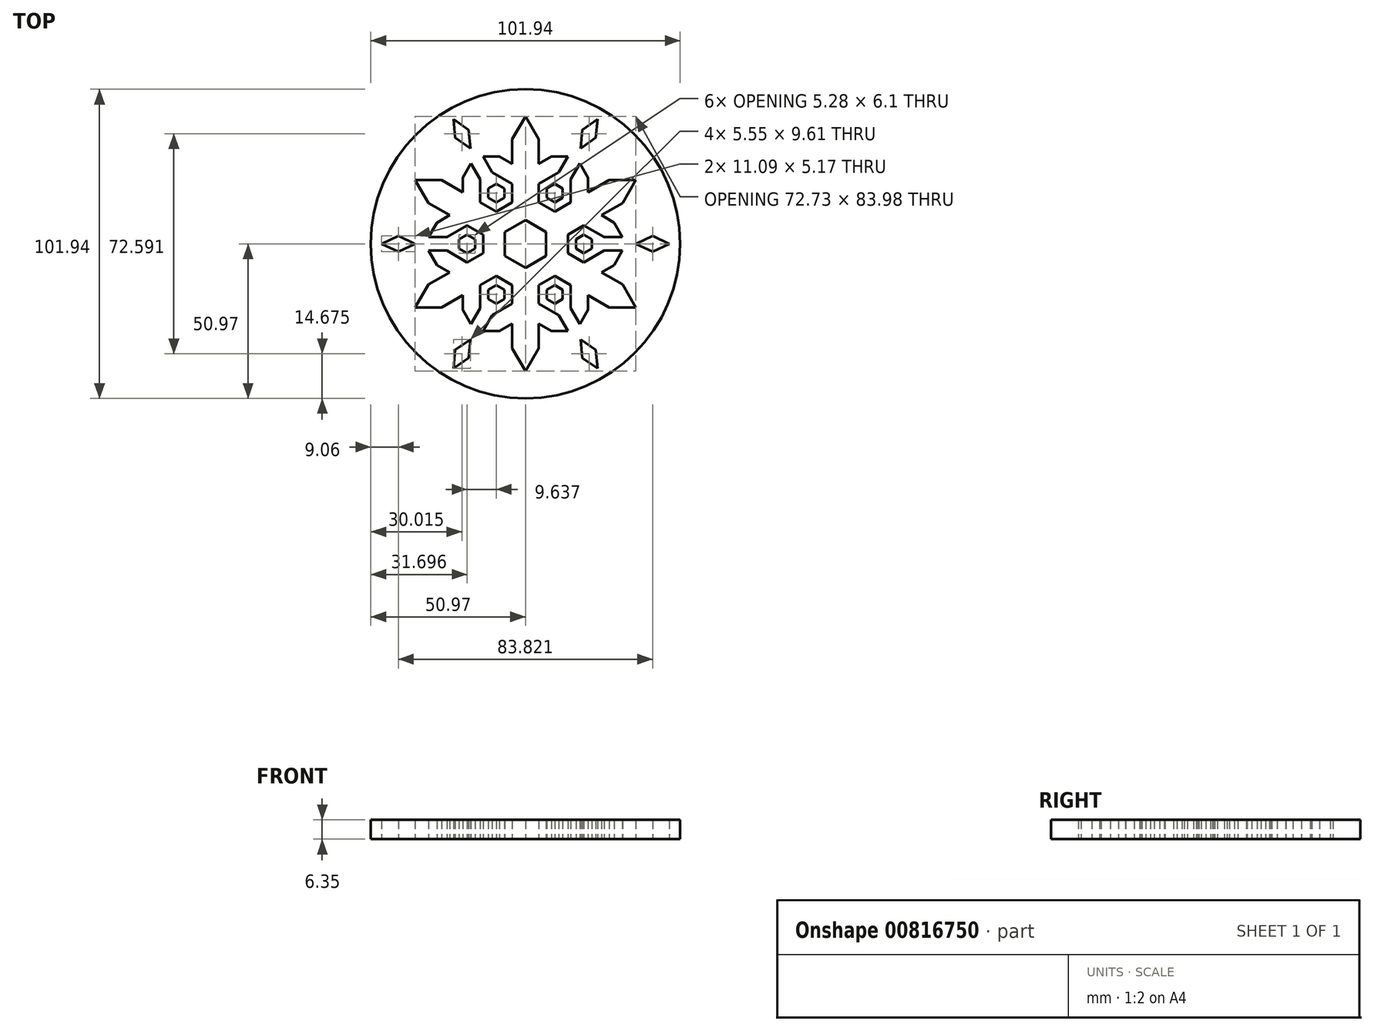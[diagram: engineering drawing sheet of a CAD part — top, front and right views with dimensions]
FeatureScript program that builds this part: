
annotation { "Feature Type Name" : "Feature", "Feature Type Description" : "" }
export const myFeature = defineFeature(function(context is Context, id is Id, definition is map)
    precondition{}
    {
        {
            var Q0;
            Q0=qCreatedBy(makeId("Top.planeOp"),FACE);
            var sketch = newSketch(context, id + "F0", { "sketchPlane" : qUnion([Q0])});
            skCircle(sketch, "E0.cCircle", {"center": v(0, 0) * mm, "radius": 41.99 * mm, "construction": true});
            skLineSegment(sketch, "E0.0", {"start": v(0, 41.99) * mm, "end": v(36.36, 21) * mm, "construction": true});
            skLineSegment(sketch, "E0.1", {"start": v(36.36, 21) * mm, "end": v(36.36, -21) * mm, "construction": true});
            skLineSegment(sketch, "E0.2", {"start": v(36.36, -21) * mm, "end": v(0, -41.99) * mm, "construction": true});
            skLineSegment(sketch, "E0.3", {"start": v(0, -41.99) * mm, "end": v(-36.36, -21) * mm, "construction": true});
            skLineSegment(sketch, "E0.4", {"start": v(-36.36, -21) * mm, "end": v(-36.36, 21) * mm, "construction": true});
            skLineSegment(sketch, "E0.5", {"start": v(-36.36, 21) * mm, "end": v(0, 41.99) * mm, "construction": true});
            skLineSegment(sketch, "E1", {"start": v(0, 41.99) * mm, "end": v(-4.36, 34.44) * mm});
            skLineSegment(sketch, "E2", {"start": v(-4.36, 34.44) * mm, "end": v(-4.36, 26.36) * mm});
            skLineSegment(sketch, "E3", {"start": v(-4.36, 26.36) * mm, "end": v(-8.55, 28.78) * mm});
            skLineSegment(sketch, "E4", {"start": v(-8.55, 28.78) * mm, "end": v(-14, 28.78) * mm});
            skLineSegment(sketch, "E5", {"start": v(-14, 28.78) * mm, "end": v(-10.98, 23.56) * mm});
            skLineSegment(sketch, "E6", {"start": v(-10.98, 23.56) * mm, "end": v(-4.36, 19.74) * mm});
            skLineSegment(sketch, "E7", {"start": v(-4.36, 19.74) * mm, "end": v(-4.36, 13.64) * mm});
            skLineSegment(sketch, "E8", {"start": v(0, 50.97) * mm, "end": v(0, -50.97) * mm, "construction": true});
            skLineSegment(sketch, "E9.MirrorCS", {"start": v(0, 41.99) * mm, "end": v(4.36, 34.44) * mm});
            skLineSegment(sketch, "E10.MirrorCS", {"start": v(4.36, 34.44) * mm, "end": v(4.36, 26.36) * mm});
            skLineSegment(sketch, "E11.MirrorCS", {"start": v(4.36, 26.36) * mm, "end": v(8.55, 28.78) * mm});
            skLineSegment(sketch, "E12.MirrorCS", {"start": v(8.55, 28.78) * mm, "end": v(14, 28.78) * mm});
            skLineSegment(sketch, "E13.MirrorCS", {"start": v(14, 28.78) * mm, "end": v(10.98, 23.56) * mm});
            skLineSegment(sketch, "E14.MirrorCS", {"start": v(4.36, 19.74) * mm, "end": v(4.36, 13.64) * mm});
            skLineSegment(sketch, "E15.MirrorCS", {"start": v(10.98, 23.56) * mm, "end": v(4.36, 19.74) * mm});
            skLineSegment(sketch, "E16", {"start": v(-25.48, -44.14) * mm, "end": v(25.48, 44.14) * mm, "construction": true});
            skLineSegment(sketch, "E17", {"start": v(-50.97, 0) * mm, "end": v(50.97, 0) * mm, "construction": true});
            skLineSegment(sketch, "E18", {"start": v(-25.48, 44.14) * mm, "end": v(25.48, -44.14) * mm, "construction": true});
            skLineSegment(sketch, "E19.MirrorCS", {"start": v(25, 9.4) * mm, "end": v(29.2, 6.99) * mm});
            skLineSegment(sketch, "E20.MirrorCS", {"start": v(25.9, 2.27) * mm, "end": v(19.27, 6.1) * mm});
            skLineSegment(sketch, "E21.MirrorCS", {"start": v(31.92, 2.27) * mm, "end": v(25.9, 2.27) * mm});
            skLineSegment(sketch, "E22.MirrorCS", {"start": v(36.36, 21) * mm, "end": v(27.65, 21) * mm});
            skLineSegment(sketch, "E23.MirrorCS", {"start": v(17.93, 26.5) * mm, "end": v(14.92, 21.3) * mm});
            skLineSegment(sketch, "E24.MirrorCS", {"start": v(20.65, 16.95) * mm, "end": v(20.65, 21.8) * mm});
            skLineSegment(sketch, "E25.MirrorCS", {"start": v(36.36, 21) * mm, "end": v(32, 13.45) * mm});
            skLineSegment(sketch, "E26.MirrorCS", {"start": v(20.65, 21.8) * mm, "end": v(17.93, 26.5) * mm});
            skLineSegment(sketch, "E27.MirrorCS", {"start": v(29.2, 6.99) * mm, "end": v(31.92, 2.27) * mm});
            skLineSegment(sketch, "E28.MirrorCS", {"start": v(14.92, 13.64) * mm, "end": v(9.64, 10.6) * mm});
            skLineSegment(sketch, "E29.MirrorCS", {"start": v(19.27, 6.1) * mm, "end": v(14, 3.05) * mm});
            skLineSegment(sketch, "E30.MirrorCS", {"start": v(14.92, 21.3) * mm, "end": v(14.92, 13.64) * mm});
            skLineSegment(sketch, "E31.MirrorCS", {"start": v(32, 13.45) * mm, "end": v(25, 9.4) * mm});
            skLineSegment(sketch, "E32.MirrorCS", {"start": v(27.65, 21) * mm, "end": v(20.65, 16.95) * mm});
            skLineSegment(sketch, "E33.MirrorCS", {"start": v(25, -9.4) * mm, "end": v(29.2, -6.99) * mm});
            skLineSegment(sketch, "E34.MirrorCS", {"start": v(27.65, -21) * mm, "end": v(20.65, -16.95) * mm});
            skLineSegment(sketch, "E35.MirrorCS", {"start": v(36.36, -21) * mm, "end": v(32, -13.45) * mm});
            skLineSegment(sketch, "E36.MirrorCS", {"start": v(31.92, -2.27) * mm, "end": v(25.9, -2.27) * mm});
            skLineSegment(sketch, "E37.MirrorCS", {"start": v(14.92, -13.64) * mm, "end": v(9.64, -10.6) * mm});
            skLineSegment(sketch, "E38.MirrorCS", {"start": v(17.93, -26.5) * mm, "end": v(14.92, -21.3) * mm});
            skLineSegment(sketch, "E39.MirrorCS", {"start": v(14.92, -21.3) * mm, "end": v(14.92, -13.64) * mm});
            skLineSegment(sketch, "E40.MirrorCS", {"start": v(25.9, -2.27) * mm, "end": v(19.27, -6.1) * mm});
            skLineSegment(sketch, "E41.MirrorCS", {"start": v(19.27, -6.1) * mm, "end": v(14, -3.05) * mm});
            skLineSegment(sketch, "E42.MirrorCS", {"start": v(20.65, -16.95) * mm, "end": v(20.65, -21.8) * mm});
            skLineSegment(sketch, "E43.MirrorCS", {"start": v(32, -13.45) * mm, "end": v(25, -9.4) * mm});
            skLineSegment(sketch, "E44.MirrorCS", {"start": v(20.65, -21.8) * mm, "end": v(17.93, -26.5) * mm});
            skLineSegment(sketch, "E45.MirrorCS", {"start": v(36.36, -21) * mm, "end": v(27.65, -21) * mm});
            skLineSegment(sketch, "E46.MirrorCS", {"start": v(29.2, -6.99) * mm, "end": v(31.92, -2.27) * mm});
            skLineSegment(sketch, "E47.MirrorCS", {"start": v(-4.36, -26.36) * mm, "end": v(-8.55, -28.78) * mm});
            skLineSegment(sketch, "E48.MirrorCS", {"start": v(-25, 9.4) * mm, "end": v(-29.2, 6.99) * mm});
            skLineSegment(sketch, "E49.MirrorCS", {"start": v(0, -41.99) * mm, "end": v(-4.36, -34.44) * mm});
            skLineSegment(sketch, "E50.MirrorCS", {"start": v(4.36, -26.36) * mm, "end": v(8.55, -28.78) * mm});
            skLineSegment(sketch, "E51.MirrorCS", {"start": v(-14.92, -21.3) * mm, "end": v(-14.92, -13.64) * mm});
            skLineSegment(sketch, "E52.MirrorCS", {"start": v(-31.92, 2.27) * mm, "end": v(-25.9, 2.27) * mm});
            skLineSegment(sketch, "E53.MirrorCS", {"start": v(8.55, -28.78) * mm, "end": v(14, -28.78) * mm});
            skLineSegment(sketch, "E54.MirrorCS", {"start": v(-20.65, -21.8) * mm, "end": v(-17.93, -26.5) * mm});
            skLineSegment(sketch, "E55.MirrorCS", {"start": v(4.36, -34.44) * mm, "end": v(4.36, -26.36) * mm});
            skLineSegment(sketch, "E56.MirrorCS", {"start": v(-29.2, 6.99) * mm, "end": v(-31.92, 2.27) * mm});
            skLineSegment(sketch, "E57.MirrorCS", {"start": v(-20.65, -16.95) * mm, "end": v(-20.65, -21.8) * mm});
            skLineSegment(sketch, "E58.MirrorCS", {"start": v(-4.36, -34.44) * mm, "end": v(-4.36, -26.36) * mm});
            skLineSegment(sketch, "E59.MirrorCS", {"start": v(-14, -28.78) * mm, "end": v(-10.98, -23.56) * mm});
            skLineSegment(sketch, "E60.MirrorCS", {"start": v(-17.93, -26.5) * mm, "end": v(-14.92, -21.3) * mm});
            skLineSegment(sketch, "E61.MirrorCS", {"start": v(14, -28.78) * mm, "end": v(10.98, -23.56) * mm});
            skLineSegment(sketch, "E62.MirrorCS", {"start": v(-31.92, -2.27) * mm, "end": v(-25.9, -2.27) * mm});
            skLineSegment(sketch, "E63.MirrorCS", {"start": v(0, -41.99) * mm, "end": v(4.36, -34.44) * mm});
            skLineSegment(sketch, "E64.MirrorCS", {"start": v(-32, 13.45) * mm, "end": v(-25, 9.4) * mm});
            skLineSegment(sketch, "E65.MirrorCS", {"start": v(-10.98, -23.56) * mm, "end": v(-4.36, -19.74) * mm});
            skLineSegment(sketch, "E66.MirrorCS", {"start": v(-25.9, 2.27) * mm, "end": v(-19.27, 6.1) * mm});
            skLineSegment(sketch, "E67.MirrorCS", {"start": v(-36.36, -21) * mm, "end": v(-32, -13.45) * mm});
            skLineSegment(sketch, "E68.MirrorCS", {"start": v(-17.93, 26.5) * mm, "end": v(-14.92, 21.3) * mm});
            skLineSegment(sketch, "E69.MirrorCS", {"start": v(-20.65, 21.8) * mm, "end": v(-17.93, 26.5) * mm});
            skLineSegment(sketch, "E70.MirrorCS", {"start": v(-20.65, 16.95) * mm, "end": v(-20.65, 21.8) * mm});
            skLineSegment(sketch, "E71.MirrorCS", {"start": v(-36.36, 21) * mm, "end": v(-27.65, 21) * mm});
            skLineSegment(sketch, "E72.MirrorCS", {"start": v(-14.92, 21.3) * mm, "end": v(-14.92, 13.64) * mm});
            skLineSegment(sketch, "E73.MirrorCS", {"start": v(-36.36, -21) * mm, "end": v(-27.65, -21) * mm});
            skLineSegment(sketch, "E74.MirrorCS", {"start": v(-36.36, 21) * mm, "end": v(-32, 13.45) * mm});
            skLineSegment(sketch, "E75.MirrorCS", {"start": v(-27.65, -21) * mm, "end": v(-20.65, -16.95) * mm});
            skLineSegment(sketch, "E76.MirrorCS", {"start": v(-27.65, 21) * mm, "end": v(-20.65, 16.95) * mm});
            skLineSegment(sketch, "E77.MirrorCS", {"start": v(-25, -9.4) * mm, "end": v(-29.2, -6.99) * mm});
            skLineSegment(sketch, "E78.MirrorCS", {"start": v(-29.2, -6.99) * mm, "end": v(-31.92, -2.27) * mm});
            skLineSegment(sketch, "E79.MirrorCS", {"start": v(-32, -13.45) * mm, "end": v(-25, -9.4) * mm});
            skLineSegment(sketch, "E80.MirrorCS", {"start": v(-8.55, -28.78) * mm, "end": v(-14, -28.78) * mm});
            skLineSegment(sketch, "E81.MirrorCS", {"start": v(-14.92, -13.64) * mm, "end": v(-9.64, -10.6) * mm});
            skLineSegment(sketch, "E82.MirrorCS", {"start": v(-19.27, -6.1) * mm, "end": v(-14, -3.05) * mm});
            skLineSegment(sketch, "E83.MirrorCS", {"start": v(-19.27, 6.1) * mm, "end": v(-14, 3.05) * mm});
            skLineSegment(sketch, "E84.MirrorCS", {"start": v(-25.9, -2.27) * mm, "end": v(-19.27, -6.1) * mm});
            skLineSegment(sketch, "E85.MirrorCS", {"start": v(4.36, -19.74) * mm, "end": v(4.36, -13.64) * mm});
            skLineSegment(sketch, "E86.MirrorCS", {"start": v(-4.36, -19.74) * mm, "end": v(-4.36, -13.64) * mm});
            skLineSegment(sketch, "E87.MirrorCS", {"start": v(-14.92, 13.64) * mm, "end": v(-9.64, 10.6) * mm});
            skLineSegment(sketch, "E88.MirrorCS", {"start": v(10.98, -23.56) * mm, "end": v(4.36, -19.74) * mm});
            skCircle(sketch, "E89", {"center": v(0, 0) * mm, "radius": 50.97 * mm});
            skLineSegment(sketch, "E90.0", {"start": v(4.36, 13.64) * mm, "end": v(9.64, 10.6) * mm});
            skLineSegment(sketch, "E90.1", {"start": v(14, 3.05) * mm, "end": v(14, -3.05) * mm});
            skLineSegment(sketch, "E90.2", {"start": v(9.64, -10.6) * mm, "end": v(4.36, -13.64) * mm});
            skLineSegment(sketch, "E90.3", {"start": v(-4.36, -13.64) * mm, "end": v(-9.64, -10.6) * mm});
            skLineSegment(sketch, "E90.4", {"start": v(-14, -3.05) * mm, "end": v(-14, 3.05) * mm});
            skLineSegment(sketch, "E90.5", {"start": v(-9.64, 10.6) * mm, "end": v(-4.36, 13.64) * mm});
            skLineSegment(sketch, "E91.0", {"start": v(0, 7.87) * mm, "end": v(6.81, 3.93) * mm});
            skLineSegment(sketch, "E91.1", {"start": v(6.81, 3.93) * mm, "end": v(6.81, -3.93) * mm});
            skLineSegment(sketch, "E91.2", {"start": v(6.81, -3.93) * mm, "end": v(0, -7.87) * mm});
            skLineSegment(sketch, "E91.3", {"start": v(0, -7.87) * mm, "end": v(-6.81, -3.93) * mm});
            skLineSegment(sketch, "E91.4", {"start": v(-6.81, -3.93) * mm, "end": v(-6.81, 3.93) * mm});
            skLineSegment(sketch, "E91.5", {"start": v(-6.81, 3.93) * mm, "end": v(0, 7.87) * mm});
            skLineSegment(sketch, "E92", {"start": v(-18.18, -31.5) * mm, "end": v(-18.72, -37.59) * mm});
            skLineSegment(sketch, "E93", {"start": v(-18.72, -37.59) * mm, "end": v(-23.73, -41.1) * mm});
            skLineSegment(sketch, "E94", {"start": v(-23.73, -41.1) * mm, "end": v(-23.2, -35) * mm});
            skLineSegment(sketch, "E95", {"start": v(-23.2, -35) * mm, "end": v(-18.18, -31.5) * mm});
            skLineSegment(sketch, "E96.MirrorCS", {"start": v(23.2, -35) * mm, "end": v(18.18, -31.5) * mm});
            skLineSegment(sketch, "E97.MirrorCS", {"start": v(18.18, -31.5) * mm, "end": v(18.72, -37.59) * mm});
            skLineSegment(sketch, "E98.MirrorCS", {"start": v(18.72, -37.59) * mm, "end": v(23.73, -41.1) * mm});
            skLineSegment(sketch, "E99.MirrorCS", {"start": v(23.73, -41.1) * mm, "end": v(23.2, -35) * mm});
            skLineSegment(sketch, "E100", {"start": v(-36.36, 21) * mm, "end": v(36.36, -21) * mm, "construction": true});
            skLineSegment(sketch, "E101.MirrorCS", {"start": v(41.91, -2.59) * mm, "end": v(36.36, 0) * mm});
            skLineSegment(sketch, "E102.MirrorCS", {"start": v(36.36, 0) * mm, "end": v(41.91, 2.59) * mm});
            skLineSegment(sketch, "E103.MirrorCS", {"start": v(41.91, 2.59) * mm, "end": v(47.46, 0) * mm});
            skLineSegment(sketch, "E104.MirrorCS", {"start": v(47.46, 0) * mm, "end": v(41.91, -2.59) * mm});
            skLineSegment(sketch, "E105", {"start": v(-36.36, -21) * mm, "end": v(36.36, 21) * mm, "construction": true});
            skLineSegment(sketch, "E106.MirrorCS", {"start": v(23.2, 35) * mm, "end": v(23.73, 41.1) * mm});
            skLineSegment(sketch, "E107.MirrorCS", {"start": v(18.18, 31.5) * mm, "end": v(23.2, 35) * mm});
            skLineSegment(sketch, "E108.MirrorCS", {"start": v(18.72, 37.59) * mm, "end": v(18.18, 31.5) * mm});
            skLineSegment(sketch, "E109.MirrorCS", {"start": v(23.73, 41.1) * mm, "end": v(18.72, 37.59) * mm});
            skLineSegment(sketch, "E110.MirrorCS", {"start": v(-23.73, 41.1) * mm, "end": v(-18.72, 37.59) * mm});
            skLineSegment(sketch, "E111.MirrorCS", {"start": v(-18.72, 37.59) * mm, "end": v(-18.18, 31.5) * mm});
            skLineSegment(sketch, "E112.MirrorCS", {"start": v(-18.18, 31.5) * mm, "end": v(-23.2, 35) * mm});
            skLineSegment(sketch, "E113.MirrorCS", {"start": v(-23.2, 35) * mm, "end": v(-23.73, 41.1) * mm});
            skLineSegment(sketch, "E114.MirrorCS", {"start": v(-36.36, 0) * mm, "end": v(-41.91, 2.59) * mm});
            skLineSegment(sketch, "E115.MirrorCS", {"start": v(-41.91, -2.59) * mm, "end": v(-36.36, 0) * mm});
            skLineSegment(sketch, "E116.MirrorCS", {"start": v(-47.46, 0) * mm, "end": v(-41.91, -2.59) * mm});
            skLineSegment(sketch, "E117.MirrorCS", {"start": v(-41.91, 2.59) * mm, "end": v(-47.46, 0) * mm});
            skLineSegment(sketch, "E118", {"start": v(-4.36, 34.44) * mm, "end": v(-27.65, 21) * mm, "construction": true});
            skLineSegment(sketch, "E119", {"start": v(-4.36, 19.74) * mm, "end": v(-14.92, 13.64) * mm, "construction": true});
            skCircle(sketch, "E120.cCircle", {"center": v(-9.64, 16.7) * mm, "radius": 3.05 * mm, "construction": true});
            skLineSegment(sketch, "E120.0", {"start": v(-7, 18.22) * mm, "end": v(-7, 15.17) * mm});
            skLineSegment(sketch, "E120.1", {"start": v(-7, 15.17) * mm, "end": v(-9.64, 13.64) * mm});
            skLineSegment(sketch, "E120.2", {"start": v(-9.64, 13.64) * mm, "end": v(-12.28, 15.17) * mm});
            skLineSegment(sketch, "E120.3", {"start": v(-12.28, 15.17) * mm, "end": v(-12.28, 18.22) * mm});
            skLineSegment(sketch, "E120.4", {"start": v(-12.28, 18.22) * mm, "end": v(-9.64, 19.74) * mm});
            skLineSegment(sketch, "E120.5", {"start": v(-9.64, 19.74) * mm, "end": v(-7, 18.22) * mm});
            skCircle(sketch, "E121.MirrorC", {"center": v(19.27, 0) * mm, "radius": 3.05 * mm, "construction": true});
            skLineSegment(sketch, "E122.MirrorCS", {"start": v(19.27, 3.05) * mm, "end": v(16.63, 1.52) * mm});
            skLineSegment(sketch, "E123.MirrorCS", {"start": v(16.63, -1.52) * mm, "end": v(19.27, -3.05) * mm});
            skLineSegment(sketch, "E124.MirrorCS", {"start": v(16.63, 1.52) * mm, "end": v(16.63, -1.52) * mm});
            skLineSegment(sketch, "E125.MirrorCS", {"start": v(19.27, -3.05) * mm, "end": v(21.91, -1.52) * mm});
            skLineSegment(sketch, "E126.MirrorCS", {"start": v(21.91, -1.52) * mm, "end": v(21.91, 1.52) * mm});
            skLineSegment(sketch, "E127.MirrorCS", {"start": v(21.91, 1.52) * mm, "end": v(19.27, 3.05) * mm});
            skLineSegment(sketch, "E128.MirrorCS", {"start": v(19.27, 6.1) * mm, "end": v(19.27, -6.1) * mm, "construction": true});
            skLineSegment(sketch, "E129", {"start": v(4.36, 19.74) * mm, "end": v(14.92, 13.64) * mm, "construction": true});
            skLineSegment(sketch, "E130", {"start": v(14.92, -13.64) * mm, "end": v(4.36, -19.74) * mm, "construction": true});
            skLineSegment(sketch, "E131", {"start": v(-4.36, -19.74) * mm, "end": v(-14.92, -13.64) * mm, "construction": true});
            skLineSegment(sketch, "E132", {"start": v(-19.27, -6.1) * mm, "end": v(-19.27, 6.1) * mm, "construction": true});
            skLineSegment(sketch, "E133", {"start": v(-9.64, 16.7) * mm, "end": v(-9.64, 10.6) * mm, "construction": true});
            skCircle(sketch, "E134.cCircle", {"center": v(9.64, 16.7) * mm, "radius": 2.64 * mm, "construction": true});
            skLineSegment(sketch, "E134.0", {"start": v(9.64, 19.74) * mm, "end": v(12.28, 18.22) * mm});
            skLineSegment(sketch, "E134.1", {"start": v(12.28, 18.22) * mm, "end": v(12.28, 15.17) * mm});
            skLineSegment(sketch, "E134.2", {"start": v(12.28, 15.17) * mm, "end": v(9.64, 13.64) * mm});
            skLineSegment(sketch, "E134.3", {"start": v(9.64, 13.64) * mm, "end": v(7, 15.17) * mm});
            skLineSegment(sketch, "E134.4", {"start": v(7, 15.17) * mm, "end": v(7, 18.22) * mm});
            skLineSegment(sketch, "E134.5", {"start": v(7, 18.22) * mm, "end": v(9.64, 19.74) * mm});
            skPoint(sketch, "E134.0.midPoint", {"position": v(10.96, 18.98) * mm});
            skCircle(sketch, "E135.cCircle", {"center": v(9.64, -16.7) * mm, "radius": 2.64 * mm, "construction": true});
            skLineSegment(sketch, "E135.0", {"start": v(12.28, -18.22) * mm, "end": v(9.64, -19.74) * mm});
            skLineSegment(sketch, "E135.1", {"start": v(9.64, -19.74) * mm, "end": v(7, -18.22) * mm});
            skLineSegment(sketch, "E135.2", {"start": v(7, -18.22) * mm, "end": v(7, -15.17) * mm});
            skLineSegment(sketch, "E135.3", {"start": v(7, -15.17) * mm, "end": v(9.64, -13.64) * mm});
            skLineSegment(sketch, "E135.4", {"start": v(9.64, -13.64) * mm, "end": v(12.28, -15.17) * mm});
            skLineSegment(sketch, "E135.5", {"start": v(12.28, -15.17) * mm, "end": v(12.28, -18.22) * mm});
            skPoint(sketch, "E135.0.midPoint", {"position": v(10.96, -18.98) * mm});
            skCircle(sketch, "E136.cCircle", {"center": v(-9.64, -16.7) * mm, "radius": 2.64 * mm, "construction": true});
            skLineSegment(sketch, "E136.0", {"start": v(-9.64, -13.64) * mm, "end": v(-7, -15.17) * mm});
            skLineSegment(sketch, "E136.1", {"start": v(-7, -15.17) * mm, "end": v(-7, -18.22) * mm});
            skLineSegment(sketch, "E136.2", {"start": v(-7, -18.22) * mm, "end": v(-9.64, -19.74) * mm});
            skLineSegment(sketch, "E136.3", {"start": v(-9.64, -19.74) * mm, "end": v(-12.28, -18.22) * mm});
            skLineSegment(sketch, "E136.4", {"start": v(-12.28, -18.22) * mm, "end": v(-12.28, -15.17) * mm});
            skLineSegment(sketch, "E136.5", {"start": v(-12.28, -15.17) * mm, "end": v(-9.64, -13.64) * mm});
            skPoint(sketch, "E136.0.midPoint", {"position": v(-8.32, -14.4) * mm});
            skCircle(sketch, "E137.cCircle", {"center": v(-19.27, 0) * mm, "radius": 2.64 * mm, "construction": true});
            skLineSegment(sketch, "E137.0", {"start": v(-21.91, -1.52) * mm, "end": v(-21.91, 1.52) * mm});
            skLineSegment(sketch, "E137.1", {"start": v(-21.91, 1.52) * mm, "end": v(-19.27, 3.05) * mm});
            skLineSegment(sketch, "E137.2", {"start": v(-19.27, 3.05) * mm, "end": v(-16.63, 1.52) * mm});
            skLineSegment(sketch, "E137.3", {"start": v(-16.63, 1.52) * mm, "end": v(-16.63, -1.52) * mm});
            skLineSegment(sketch, "E137.4", {"start": v(-16.63, -1.52) * mm, "end": v(-19.27, -3.05) * mm});
            skLineSegment(sketch, "E137.5", {"start": v(-19.27, -3.05) * mm, "end": v(-21.91, -1.52) * mm});
            skPoint(sketch, "E137.0.midPoint", {"position": v(-21.91, 0) * mm});
            skLineSegment(sketch, "E138", {"start": v(9.64, 16.7) * mm, "end": v(4.36, 13.64) * mm, "construction": true});
            skLineSegment(sketch, "E139", {"start": v(19.27, 0) * mm, "end": v(14, 3.05) * mm, "construction": true});
            skLineSegment(sketch, "E140", {"start": v(-19.27, 0) * mm, "end": v(-14, -3.05) * mm, "construction": true});
            skLineSegment(sketch, "E141", {"start": v(-9.64, -16.7) * mm, "end": v(-4.36, -13.64) * mm, "construction": true});
            skLineSegment(sketch, "E142", {"start": v(9.64, -16.7) * mm, "end": v(9.64, -10.6) * mm, "construction": true});
            skSolve(sketch);
        }
        {
            var Q0;
            Q0=makeQuery(id+"F0.imprint","IMPRINT",FACE,{"disambiguationData":[TD([[makeQuery(id+"F0.imprint","IMPRINT",EDGE,{"derivedFrom":sQuery(id+"F0.wireOp",EDGE,"E1")}),-1.0]])]});
            var Q1;
            {var subQ8=sQuery(id+"F0.wireOp",EDGE,"E91.0");Q1=makeQuery(id+"F0.imprint","IMPRINT",FACE,{"disambiguationData":[TD([[makeQuery(id+"F0.imprint","IMPRINT",EDGE,{"derivedFrom":subQ8}),-1.0]])]});}
            extrude(context, id + "F1", {"entities" : qUnion([Q0, Q1]), "depth" : 6.35 * mm, "offsetDistance" : 25.4 * mm});
        }
    });
